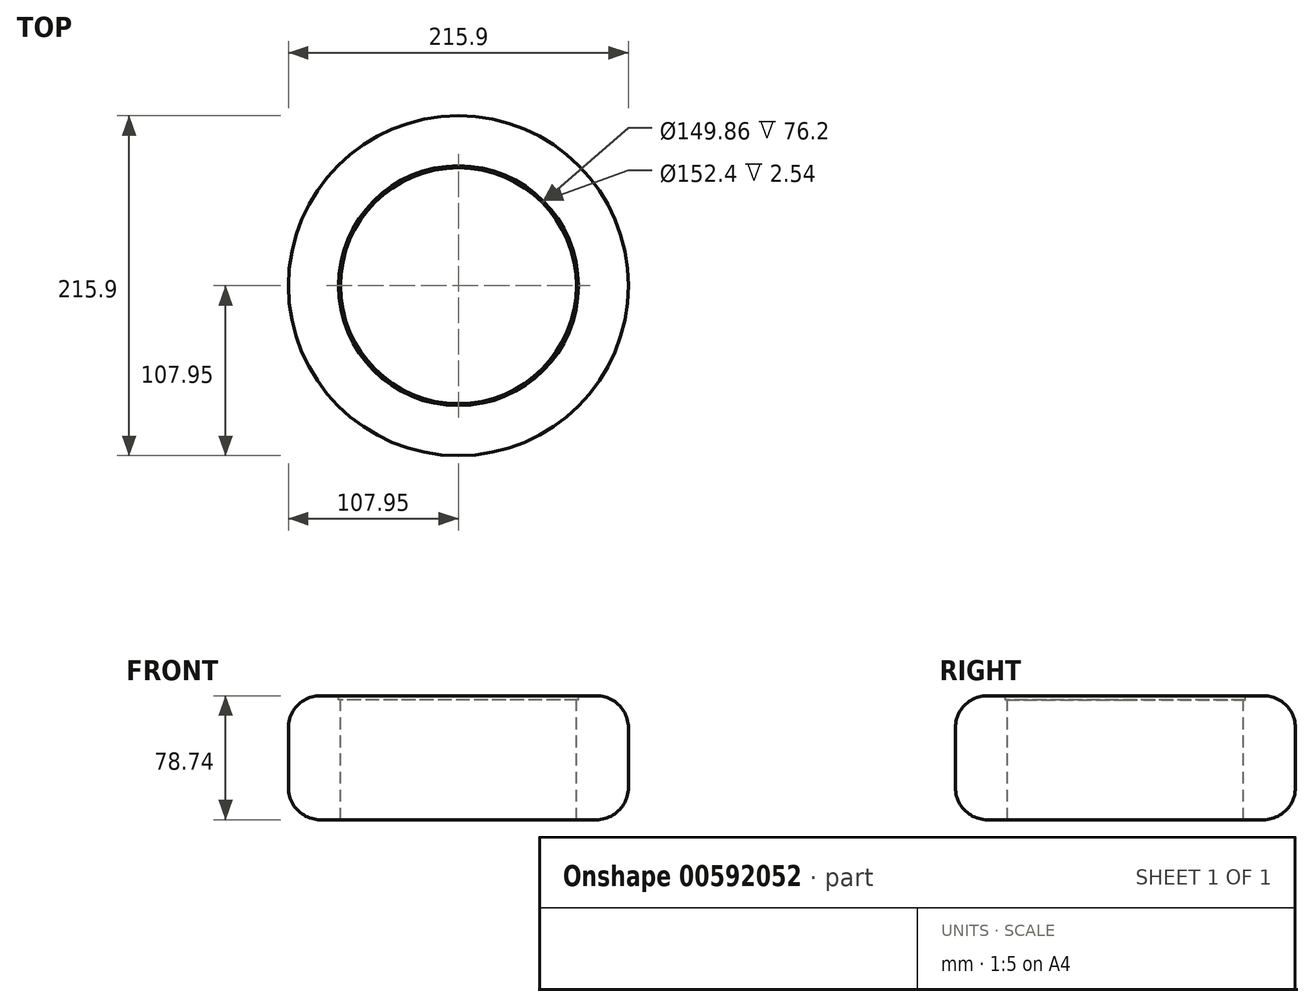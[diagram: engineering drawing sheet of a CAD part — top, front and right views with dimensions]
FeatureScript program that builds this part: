
annotation { "Feature Type Name" : "Feature", "Feature Type Description" : "" }
export const myFeature = defineFeature(function(context is Context, id is Id, definition is map)
    precondition{}
    {
        {
            var Q0;
            Q0=qCreatedBy(makeId("Top.planeOp"),FACE);
            var sketch = newSketch(context, id + "F0", { "sketchPlane" : qUnion([Q0])});
            skCircle(sketch, "E0", {"center": v(0, 0) * mm, "radius": 74.93 * mm});
            skCircle(sketch, "E1", {"center": v(0, 0) * mm, "radius": 107.95 * mm});
            skSolve(sketch);
        }
        {
            var Q0;
            Q0=makeQuery(id+"F0.imprint","IMPRINT",FACE,{"disambiguationData":[TD([[makeQuery(id+"F0.imprint","IMPRINT",EDGE,{"derivedFrom":sQuery(id+"F0.wireOp",EDGE,"E0")}),-1.0]])]});
            extrude(context, id + "F1", {"entities" : qUnion([Q0]), "oppositeDirection" : true, "depth" : 76.2 * mm, "offsetDistance" : 25.4 * mm, "hasSecondDirection" : true, "secondDirectionOppositeDirection" : false, "secondDirectionDepth" : 2.54 * mm});
        }
        {
            var Q0;
            Q0=makeQuery(id+"F1.opExtrude","CAP_FACE",FACE,{"disambiguationData":[OSD([sQuery(id+"F0.wireOp",EDGE,"E0"),sQuery(id+"F0.wireOp",EDGE,"E1")])],"isStart":true});
            var sketch = newSketch(context, id + "F2", { "sketchPlane" : qUnion([Q0])});
            skCircle(sketch, "E2", {"center": v(0, 0) * mm, "radius": 76.2 * mm});
            skSolve(sketch);
        }
        {
            var Q0;
            Q0=makeQuery(id+"F2.imprint","IMPRINT",FACE,{"disambiguationData":[TD([[makeQuery(id+"F2.imprint","IMPRINT",EDGE,{"derivedFrom":sQuery(id+"F2.wireOp",EDGE,"E2")}),1.0]])]});
            extrude(context, id + "F3", {"entities" : qUnion([Q0]), "operationType" : NewBodyOperationType.REMOVE, "oppositeDirection" : true, "depth" : 2.54 * mm, "offsetDistance" : 25.4 * mm});
        }
        {
            var Q0;
            Q0=makeQuery(id+"F1.opExtrude","CAP_EDGE",EDGE,{"disambiguationData":[OSD([sQuery(id+"F0.wireOp",EDGE,"E1")])],"isStart":true});
            var Q1;
            Q1=makeQuery(id+"F1.opExtrude","CAP_EDGE",EDGE,{"disambiguationData":[OSD([sQuery(id+"F0.wireOp",EDGE,"E1")])],"isStart":false});
            fillet(context, id + "F4", {"entities" : qUnion([Q0, Q1]), "radius" : 20.32 * mm, "tangentPropagation" : true, "allowEdgeOverflow" : false});
        }
    });
